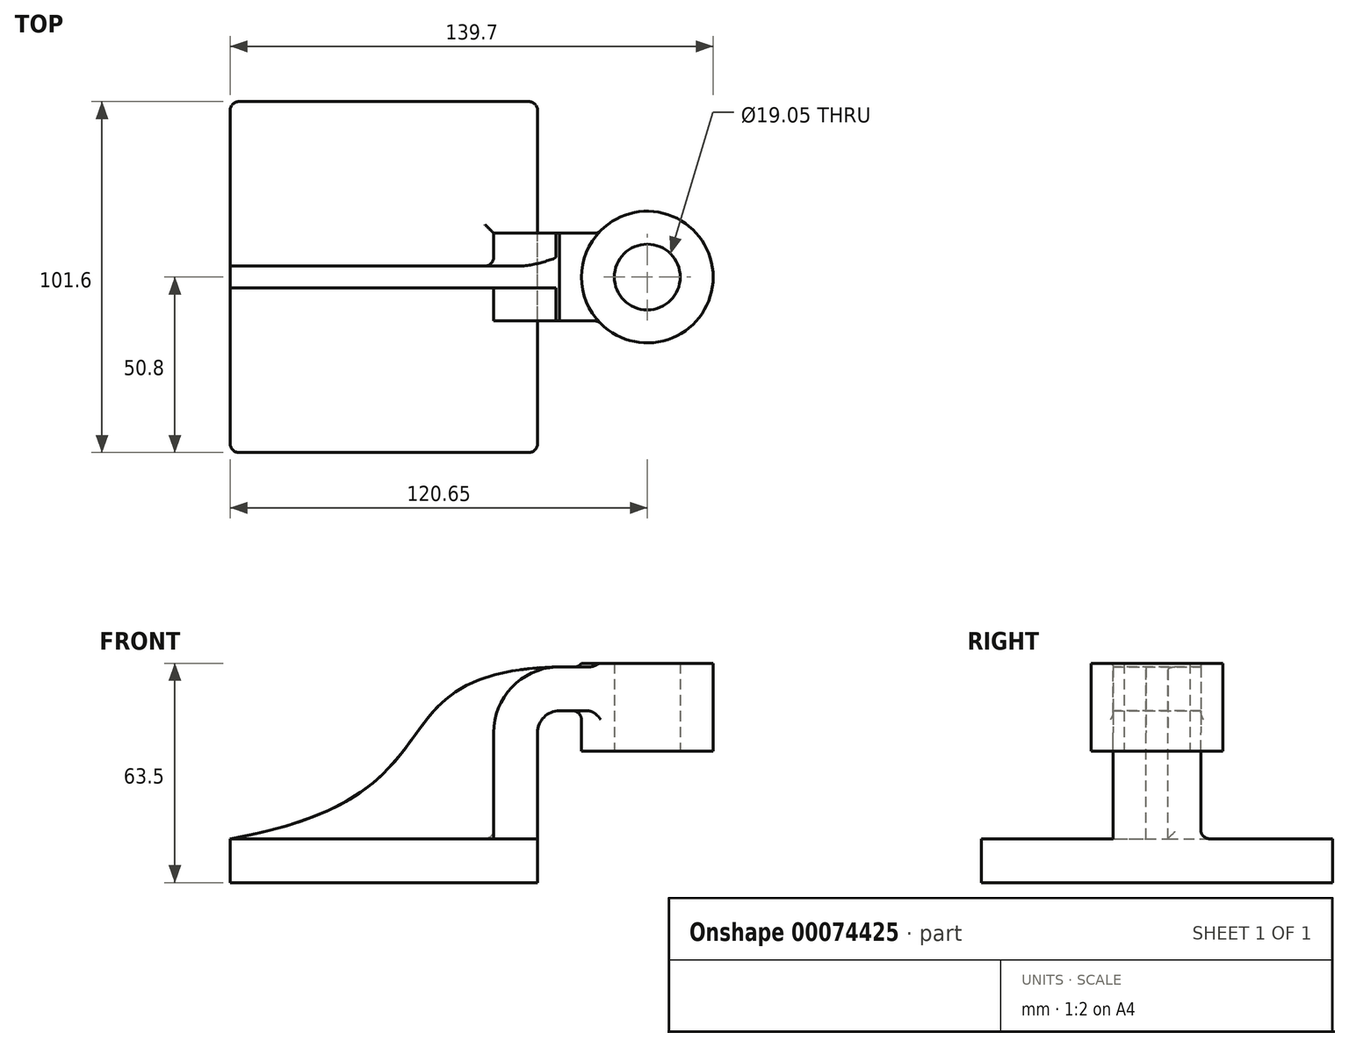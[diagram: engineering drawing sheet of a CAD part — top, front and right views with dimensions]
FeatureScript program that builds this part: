
annotation { "Feature Type Name" : "Feature", "Feature Type Description" : "" }
export const myFeature = defineFeature(function(context is Context, id is Id, definition is map)
    precondition{}
    {
        {
            var Q0;
            Q0=qCreatedBy(makeId("Front.planeOp"),FACE);
            var sketch = newSketch(context, id + "F0", { "sketchPlane" : qUnion([Q0])});
            skLineSegment(sketch, "E0.rect.bottom", {"start": v(-44.45, -6.35) * mm, "end": v(44.45, -6.35) * mm});
            skLineSegment(sketch, "E0.rect.top", {"start": v(-44.45, 6.35) * mm, "end": v(44.45, 6.35) * mm});
            skLineSegment(sketch, "E0.rect.left", {"start": v(-44.45, -6.35) * mm, "end": v(-44.45, 6.35) * mm});
            skLineSegment(sketch, "E0.rect.right", {"start": v(44.45, -6.35) * mm, "end": v(44.45, 6.35) * mm});
            skPoint(sketch, "E0.rect.middle", {"position": v(0, 0) * mm});
            skLineSegment(sketch, "E1.rect.bottom", {"start": v(76.2, 31.75) * mm, "end": v(57.15, 31.75) * mm});
            skLineSegment(sketch, "E1.rect.top", {"start": v(76.2, 57.15) * mm, "end": v(57.15, 57.15) * mm});
            skLineSegment(sketch, "E1.rect.left", {"start": v(76.2, 31.75) * mm, "end": v(76.2, 57.15) * mm});
            skLineSegment(sketch, "E1.rect.right", {"start": v(57.15, 31.75) * mm, "end": v(57.15, 57.15) * mm});
            skLineSegment(sketch, "E2", {"start": v(44.45, 6.35) * mm, "end": v(44.45, 37.04) * mm});
            skLineSegment(sketch, "E3", {"start": v(50.8, 43.4) * mm, "end": v(72.75, 43.4) * mm});
            skPoint(sketch, "E4.visualSharp", {"position": v(44.45, 43.4) * mm});
            skArc(sketch, "E4.filletArc", {"start": v(50.8, 43.4) * mm, "mid": v(46.3, 41.53) * mm, "end": v(44.45, 37.04) * mm});
            skLineSegment(sketch, "E5.0", {"start": v(50.8, 56.1) * mm, "end": v(72.75, 56.1) * mm});
            skArc(sketch, "E5.1", {"start": v(50.8, 56.1) * mm, "mid": v(37.33, 50.51) * mm, "end": v(31.75, 37.04) * mm});
            skLineSegment(sketch, "E5.2", {"start": v(31.75, 6.35) * mm, "end": v(31.75, 37.04) * mm});
            skFitSpline(sketch, "E6", {"points": [v(-44.45, 6.35) * mm, v(50.8, 56.1) * mm], "startDerivative": vector(212.71, 36.86) * mm, "endDerivative": vector(171.72, 3.78) * mm});
            skLineSegment(sketch, "E7", {"start": v(72.75, 56.1) * mm, "end": v(72.75, 43.4) * mm});
            skLineSegment(sketch, "E8", {"start": v(66.67, 57.15) * mm, "end": v(66.67, 31.75) * mm});
            skSolve(sketch);
        }
        {
            var Q0;
            Q0=makeQuery(id+"F0.imprint","IMPRINT",FACE,{"disambiguationData":[TD([[makeQuery(id+"F0.imprint","IMPRINT",EDGE,{"derivedFrom":sQuery(id+"F0.wireOp",EDGE,"E0.rect.bottom")}),1.0]])]});
            extrude(context, id + "F1", {"entities" : qUnion([Q0]), "endBound" : BoundingType.SYMMETRIC, "depth" : 101.6 * mm});
        }
        {
            var Q0;
            {var subQ3=sQuery(id+"F0.wireOp",EDGE,"E5.2");var subQ5=sQuery(id+"F0.wireOp",EDGE,"E5.1");var subQ6=makeQuery(id+"F0.imprint","INTERSECT",VERTEX,{"derivedFrom":[subQ5,subQ3]});Q0=makeQuery(id+"F0.imprint","IMPRINT",FACE,{"disambiguationData":[TD([[makeQuery(id+"F0.imprint","IMPRINT",EDGE,{"disambiguationData":[TD([[subQ6,1.0]])],"derivedFrom":subQ5}),-1.0]])]});}
            extrude(context, id + "F2", {"entities" : qUnion([Q0]), "operationType" : NewBodyOperationType.ADD, "endBound" : BoundingType.SYMMETRIC, "depth" : 6.35 * mm});
        }
        {
            var Q0;
            {var subQ4=sQuery(id+"F0.wireOp",EDGE,"E2");Q0=makeQuery(id+"F0.imprint","IMPRINT",FACE,{"disambiguationData":[TD([[makeQuery(id+"F0.imprint","IMPRINT",EDGE,{"derivedFrom":subQ4}),1.0]])]});}
            var Q1;
            {var subQ0=sQuery(id+"F0.wireOp",EDGE,"E3");var subQ1=sQuery(id+"F0.wireOp",EDGE,"E1.rect.right");var subQ2=makeQuery(id+"F0.imprint","INTERSECT",VERTEX,{"derivedFrom":[subQ1,subQ0]});Q1=makeQuery(id+"F0.imprint","IMPRINT",FACE,{"disambiguationData":[TD([[makeQuery(id+"F0.imprint","IMPRINT",EDGE,{"disambiguationData":[TD([[subQ2,-1.0]])],"derivedFrom":subQ1}),-1.0]])]});}
            extrude(context, id + "F3", {"entities" : qUnion([Q0, Q1]), "operationType" : NewBodyOperationType.ADD, "endBound" : BoundingType.SYMMETRIC, "depth" : 25.4 * mm});
        }
        {
            var Q0;
            {var subQ0=sQuery(id+"F0.wireOp",EDGE,"E1.rect.right");var subQ1=sQuery(id+"F0.wireOp",EDGE,"E1.rect.top");var subQ2=makeQuery(id+"F0.imprint","INTERSECT",VERTEX,{"derivedFrom":[subQ1,subQ0]});Q0=makeQuery(id+"F0.imprint","IMPRINT",FACE,{"disambiguationData":[TD([[makeQuery(id+"F0.imprint","IMPRINT",EDGE,{"disambiguationData":[TD([[subQ2,1.0]])],"derivedFrom":subQ1}),1.0]])]});}
            var Q1;
            {var subQ0=sQuery(id+"F0.wireOp",EDGE,"E3");var subQ1=sQuery(id+"F0.wireOp",EDGE,"E1.rect.right");var subQ2=makeQuery(id+"F0.imprint","INTERSECT",VERTEX,{"derivedFrom":[subQ1,subQ0]});Q1=makeQuery(id+"F0.imprint","IMPRINT",FACE,{"disambiguationData":[TD([[makeQuery(id+"F0.imprint","IMPRINT",EDGE,{"disambiguationData":[TD([[subQ2,-1.0]])],"derivedFrom":subQ1}),-1.0]])]});}
            var Q2;
            {var subQ0=sQuery(id+"F0.wireOp",EDGE,"E1.rect.right");var subQ1=sQuery(id+"F0.wireOp",EDGE,"E1.rect.bottom");var subQ2=makeQuery(id+"F0.imprint","INTERSECT",VERTEX,{"derivedFrom":[subQ1,subQ0]});Q2=makeQuery(id+"F0.imprint","IMPRINT",FACE,{"disambiguationData":[TD([[makeQuery(id+"F0.imprint","IMPRINT",EDGE,{"disambiguationData":[TD([[subQ2,1.0]])],"derivedFrom":subQ1}),-1.0]])]});}
            var Q3;
            Q3=sQuery(id+"F0.wireOp",EDGE,"E1.rect.left");
            revolve(context, id + "F4", {"operationType" : NewBodyOperationType.ADD, "entities" : qUnion([Q0, Q1, Q2]), "axis" : qUnion([Q3]), "revolveType" : RevolveType.FULL});
        }
        {
            var Q0;
            Q0=makeQuery(id+"F1.opExtrude","CAP_EDGE",EDGE,{"disambiguationData":[OSD([sQuery(id+"F0.wireOp",EDGE,"E0.rect.left")])],"isStart":false});
            var Q1;
            Q1=makeQuery(id+"F1.opExtrude","CAP_EDGE",EDGE,{"disambiguationData":[OSD([sQuery(id+"F0.wireOp",EDGE,"E0.rect.right")])],"isStart":false});
            var Q2;
            Q2=makeQuery(id+"F1.opExtrude","CAP_EDGE",EDGE,{"disambiguationData":[OSD([sQuery(id+"F0.wireOp",EDGE,"E0.rect.right")])],"isStart":true});
            var Q3;
            Q3=makeQuery(id+"F1.opExtrude","CAP_EDGE",EDGE,{"disambiguationData":[OSD([sQuery(id+"F0.wireOp",EDGE,"E0.rect.left")])],"isStart":true});
            var Q4;
            Q4=makeQuery(id+"F3.opExtrude","CAP_EDGE",EDGE,{"disambiguationData":[OSD([sQuery(id+"F0.wireOp",EDGE,"E0.rect.top")])],"isStart":true});
            var Q5;
            Q5=makeQuery(id+"F3.opExtrude","CAP_EDGE",EDGE,{"disambiguationData":[OSD([sQuery(id+"F0.wireOp",EDGE,"E0.rect.top")])],"isStart":false});
            var Q6;
            {var subQ0=sQuery(id+"F0.wireOp",EDGE,"E0.rect.top");var subQ1=sQuery(id+"F0.wireOp",EDGE,"E6");var subQ2=sQuery(id+"F0.wireOp",EDGE,"E5.2");var subQ3=sQuery(id+"F0.wireOp",EDGE,"E5.1");Q6=makeQuery(id+"F3.boolean.opBoolean","SPLIT",EDGE,{"disambiguationData":[TD([makeQuery(id+"F2.opExtrude","CAP_FACE",FACE,{"disambiguationData":[OSD([subQ0,subQ3,subQ2,subQ1])],"isStart":false})])],"derivedFrom":makeQuery(id+"F3.opExtrude","SWEPT_EDGE",EDGE,{"disambiguationData":[OSD([subQ0,subQ2])]})});}
            var Q7;
            {var subQ0=sQuery(id+"F0.wireOp",EDGE,"E0.rect.top");var subQ1=sQuery(id+"F0.wireOp",EDGE,"E6");var subQ2=sQuery(id+"F0.wireOp",EDGE,"E5.2");var subQ3=sQuery(id+"F0.wireOp",EDGE,"E5.1");Q7=makeQuery(id+"F3.boolean.opBoolean","SPLIT",EDGE,{"disambiguationData":[TD([makeQuery(id+"F2.opExtrude","CAP_FACE",FACE,{"disambiguationData":[OSD([subQ0,subQ3,subQ2,subQ1])],"isStart":true})])],"derivedFrom":makeQuery(id+"F3.opExtrude","SWEPT_EDGE",EDGE,{"disambiguationData":[OSD([subQ0,subQ2])]})});}
            var Q8;
            Q8=makeQuery(id+"F2.opExtrude","CAP_EDGE",EDGE,{"disambiguationData":[OSD([sQuery(id+"F0.wireOp",EDGE,"E0.rect.top")])],"isStart":true});
            var Q9;
            Q9=makeQuery(id+"F2.opExtrude","CAP_EDGE",EDGE,{"disambiguationData":[OSD([sQuery(id+"F0.wireOp",EDGE,"E5.2")])],"isStart":true});
            var Q10;
            Q10=makeQuery(id+"F2.opExtrude","CAP_EDGE",EDGE,{"disambiguationData":[OSD([sQuery(id+"F0.wireOp",EDGE,"E5.1")])],"isStart":true});
            var Q11;
            Q11=makeQuery(id+"F2.opExtrude","CAP_EDGE",EDGE,{"disambiguationData":[OSD([sQuery(id+"F0.wireOp",EDGE,"E0.rect.top")])],"isStart":false});
            var Q12;
            Q12=makeQuery(id+"F2.opExtrude","CAP_EDGE",EDGE,{"disambiguationData":[OSD([sQuery(id+"F0.wireOp",EDGE,"E5.1")])],"isStart":false});
            var Q13;
            Q13=makeQuery(id+"F2.opExtrude","CAP_EDGE",EDGE,{"disambiguationData":[OSD([sQuery(id+"F0.wireOp",EDGE,"E5.2")])],"isStart":false});
            var Q14;
            Q14=makeQuery(id+"F4.boolean.opBoolean","INTERSECT",EDGE,{"derivedFrom":[makeQuery(id+"F3.opExtrude","SWEPT_FACE",FACE,{"disambiguationData":[OSD([sQuery(id+"F0.wireOp",EDGE,"E5.0")])]}),makeQuery(id+"F4.opRevolve","SWEPT_FACE",FACE,{"disambiguationData":[OSD([sQuery(id+"F0.wireOp",EDGE,"E1.rect.right")])]})]});
            var Q15;
            Q15=makeQuery(id+"F4.boolean.opBoolean","INTERSECT",EDGE,{"derivedFrom":[makeQuery(id+"F3.opExtrude","SWEPT_FACE",FACE,{"disambiguationData":[OSD([sQuery(id+"F0.wireOp",EDGE,"E3")])]}),makeQuery(id+"F4.opRevolve","SWEPT_FACE",FACE,{"disambiguationData":[OSD([sQuery(id+"F0.wireOp",EDGE,"E1.rect.right")])]})]});
            var Q16;
            Q16=makeQuery(id+"F4.boolean.opBoolean","INTERSECT",EDGE,{"derivedFrom":[makeQuery(id+"F3.opExtrude","CAP_FACE",FACE,{"disambiguationData":[OSD([sQuery(id+"F0.wireOp",EDGE,"E0.rect.top"),sQuery(id+"F0.wireOp",EDGE,"E2"),sQuery(id+"F0.wireOp",EDGE,"E3"),sQuery(id+"F0.wireOp",EDGE,"E4.filletArc"),sQuery(id+"F0.wireOp",EDGE,"E5.0"),sQuery(id+"F0.wireOp",EDGE,"E5.1"),sQuery(id+"F0.wireOp",EDGE,"E5.2"),sQuery(id+"F0.wireOp",EDGE,"E6"),sQuery(id+"F0.wireOp",EDGE,"E7")])],"isStart":true}),makeQuery(id+"F4.opRevolve","SWEPT_FACE",FACE,{"disambiguationData":[OSD([sQuery(id+"F0.wireOp",EDGE,"E1.rect.right")])]})]});
            var Q17;
            Q17=makeQuery(id+"F4.boolean.opBoolean","INTERSECT",EDGE,{"derivedFrom":[makeQuery(id+"F3.opExtrude","CAP_FACE",FACE,{"disambiguationData":[OSD([sQuery(id+"F0.wireOp",EDGE,"E0.rect.top"),sQuery(id+"F0.wireOp",EDGE,"E2"),sQuery(id+"F0.wireOp",EDGE,"E3"),sQuery(id+"F0.wireOp",EDGE,"E4.filletArc"),sQuery(id+"F0.wireOp",EDGE,"E5.0"),sQuery(id+"F0.wireOp",EDGE,"E5.1"),sQuery(id+"F0.wireOp",EDGE,"E5.2"),sQuery(id+"F0.wireOp",EDGE,"E6"),sQuery(id+"F0.wireOp",EDGE,"E7")])],"isStart":false}),makeQuery(id+"F4.opRevolve","SWEPT_FACE",FACE,{"disambiguationData":[OSD([sQuery(id+"F0.wireOp",EDGE,"E1.rect.right")])]})]});
            fillet(context, id + "F5", {"entities" : qUnion([Q0, Q1, Q2, Q3, Q4, Q5, Q6, Q7, Q8, Q9, Q10, Q11, Q12, Q13, Q14, Q15, Q16, Q17]), "radius" : 2.54 * mm, "tangentPropagation" : true, "allowEdgeOverflow" : false});
        }
    });
